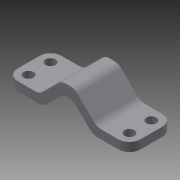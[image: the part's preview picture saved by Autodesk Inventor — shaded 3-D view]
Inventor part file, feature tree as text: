
AUTODESK INVENTOR PART (.ipt)
format: ipt  version: 2013 (Build 170138000, 138)  size: 129,536 bytes
history: native  units: mm
features: fillet x2, sketch x2, extrude x1, hole x1, mirror x1
ambient origin geometry x8: Origin, YZ Plane, XZ Plane, XY Plane, X Axis, Y Axis, Z Axis, Center Point
bodies: Solid1 (feature_tree)
feature tree (7):
  extrude  "Extrusion1"  Depth=4.0mm
  hole  "Hole3"  [1 undecoded]
  fillet  "Fillet4"  Radius=10.0mm
  mirror  "Mirror3"
  fillet  "Fillet5"  Radius=10.0mm
  sketch  "Sketch1"  dims[d7=15.0mm d9=4.0mm]
  sketch  "Sketch4"  dims[d11=20.0mm d12=0.0mm d28=5.0mm d29=10.0mm d30=4.5mm d31=6.0mm d32=9.4mm d33=2.0mm d34=90.0deg d35=8.0mm d36=20.594885mm d38=10.0mm d39=4.0mm d40=5.0mm d42=5.0mm d43=5.0mm]
note: 1 required parameter value undecoded (feature->parameter linkage not recoverable at this tier; creation-order binding heuristic only, values carry confidence <= 0.55)
